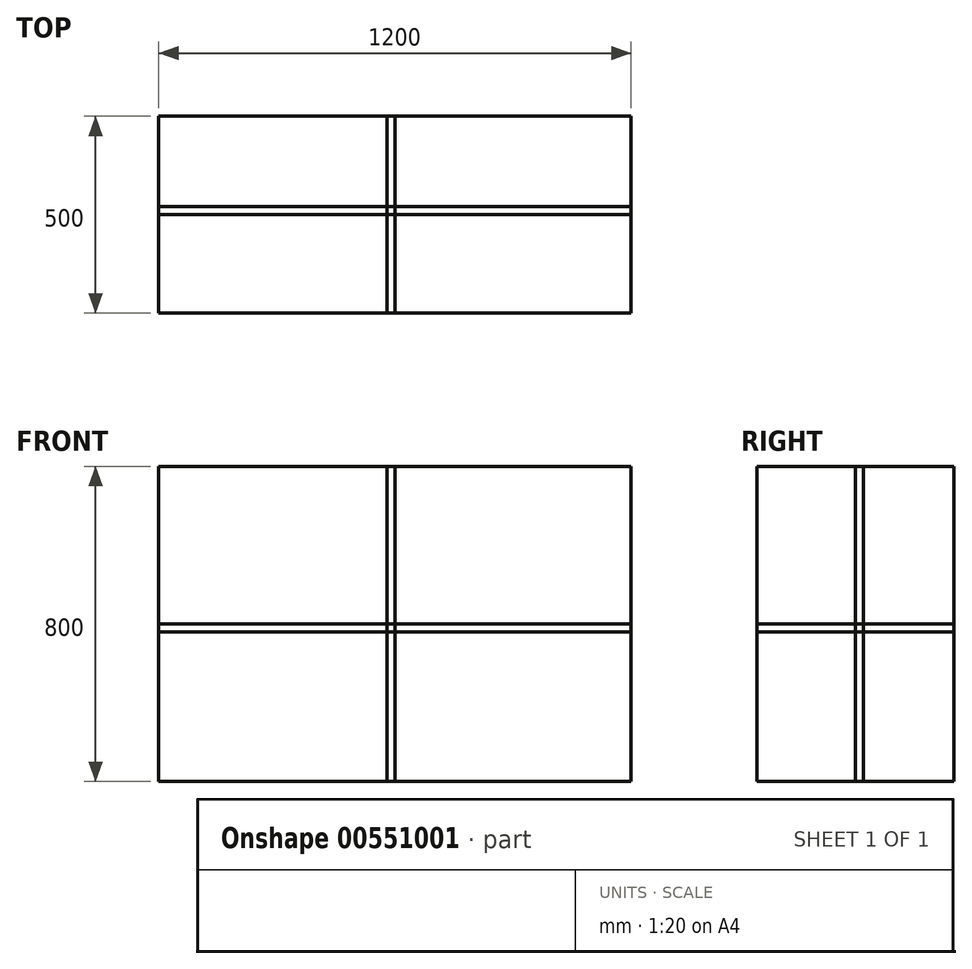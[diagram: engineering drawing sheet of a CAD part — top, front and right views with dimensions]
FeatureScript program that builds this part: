
annotation { "Feature Type Name" : "Feature", "Feature Type Description" : "" }
export const myFeature = defineFeature(function(context is Context, id is Id, definition is map)
    precondition{}
    {
        {
            var Q0;
            Q0=qCreatedBy(makeId("Top.planeOp"),FACE);
            var sketch = newSketch(context, id + "F0", { "sketchPlane" : qUnion([Q0])});
            skLineSegment(sketch, "E0.bottom", {"start": v(600, 250) * mm, "end": v(-600, 250) * mm});
            skLineSegment(sketch, "E0.top", {"start": v(600, -250) * mm, "end": v(-600, -250) * mm});
            skLineSegment(sketch, "E0.left", {"start": v(600, 250) * mm, "end": v(600, -250) * mm});
            skLineSegment(sketch, "E0.right", {"start": v(-600, 250) * mm, "end": v(-600, -250) * mm});
            skPoint(sketch, "E0.middle", {"position": v(0, 0) * mm});
            skSolve(sketch);
        }
        {
            var Q0;
            Q0 = qSketchRegion(id + "F0", true);
            extrude(context, id + "F1", {"entities" : qUnion([Q0]), "oppositeDirection" : true, "depth" : 20 * mm, "offsetDistance" : 25 * mm});
        }
        {
            var Q0;
            Q0=qCreatedBy(makeId("Top.planeOp"),FACE);
            var sketch = newSketch(context, id + "F2", { "sketchPlane" : qUnion([Q0])});
            skLineSegment(sketch, "E1.bottom", {"start": v(600, -250) * mm, "end": v(-600, -250) * mm});
            skLineSegment(sketch, "E1.top", {"start": v(600, 250) * mm, "end": v(-600, 250) * mm});
            skLineSegment(sketch, "E1.left", {"start": v(600, -250) * mm, "end": v(600, 250) * mm});
            skLineSegment(sketch, "E1.right", {"start": v(-600, -250) * mm, "end": v(-600, 250) * mm});
            skPoint(sketch, "E1.middle", {"position": v(0, 0) * mm});
            skSolve(sketch);
        }
        {
            var Q0;
            Q0 = qSketchRegion(id + "F2", true);
            extrude(context, id + "F3", {"entities" : qUnion([Q0]), "oppositeDirection" : true, "depth" : 20 * mm, "offsetDistance" : 25 * mm});
        }
        {
            var Q0;
            Q0=qCreatedBy(makeId("Front.planeOp"),FACE);
            var sketch = newSketch(context, id + "F4", { "sketchPlane" : qUnion([Q0])});
            skLineSegment(sketch, "E2.bottom", {"start": v(600, -400) * mm, "end": v(-600, -400) * mm});
            skLineSegment(sketch, "E2.top", {"start": v(600, 400) * mm, "end": v(-600, 400) * mm});
            skLineSegment(sketch, "E2.left", {"start": v(600, -400) * mm, "end": v(600, 400) * mm});
            skLineSegment(sketch, "E2.right", {"start": v(-600, -400) * mm, "end": v(-600, 400) * mm});
            skPoint(sketch, "E2.middle", {"position": v(0, 0) * mm});
            skSolve(sketch);
        }
        {
            var Q0;
            Q0 = qSketchRegion(id + "F4", true);
            extrude(context, id + "F5", {"entities" : qUnion([Q0]), "oppositeDirection" : true, "depth" : 20 * mm, "offsetDistance" : 25 * mm});
        }
        {
            var Q0;
            Q0=qCreatedBy(makeId("Front.planeOp"),FACE);
            var sketch = newSketch(context, id + "F6", { "sketchPlane" : qUnion([Q0])});
            skLineSegment(sketch, "E3.bottom", {"start": v(600, -400) * mm, "end": v(-600, -400) * mm});
            skLineSegment(sketch, "E3.top", {"start": v(600, 400) * mm, "end": v(-600, 400) * mm});
            skLineSegment(sketch, "E3.left", {"start": v(600, -400) * mm, "end": v(600, 400) * mm});
            skLineSegment(sketch, "E3.right", {"start": v(-600, -400) * mm, "end": v(-600, 400) * mm});
            skPoint(sketch, "E3.middle", {"position": v(0, 0) * mm});
            skSolve(sketch);
        }
        {
            var Q0;
            Q0 = qSketchRegion(id + "F6", true);
            extrude(context, id + "F7", {"entities" : qUnion([Q0]), "oppositeDirection" : true, "depth" : 20 * mm, "offsetDistance" : 25 * mm});
        }
        {
            var Q0;
            Q0=qCreatedBy(makeId("Right.planeOp"),FACE);
            var sketch = newSketch(context, id + "F8", { "sketchPlane" : qUnion([Q0])});
            skLineSegment(sketch, "E4.bottom", {"start": v(250, -400) * mm, "end": v(-250, -400) * mm});
            skLineSegment(sketch, "E4.top", {"start": v(250, 400) * mm, "end": v(-250, 400) * mm});
            skLineSegment(sketch, "E4.left", {"start": v(250, -400) * mm, "end": v(250, 400) * mm});
            skLineSegment(sketch, "E4.right", {"start": v(-250, -400) * mm, "end": v(-250, 400) * mm});
            skPoint(sketch, "E4.middle", {"position": v(0, 0) * mm});
            skSolve(sketch);
        }
        {
            var Q0;
            Q0 = qSketchRegion(id + "F8", true);
            extrude(context, id + "F9", {"entities" : qUnion([Q0]), "oppositeDirection" : true, "depth" : 20 * mm, "offsetDistance" : 25 * mm});
        }
        {
            var Q0;
            Q0=qCreatedBy(makeId("Right.planeOp"),FACE);
            var sketch = newSketch(context, id + "F10", { "sketchPlane" : qUnion([Q0])});
            skLineSegment(sketch, "E5.bottom", {"start": v(250, -400) * mm, "end": v(-250, -400) * mm});
            skLineSegment(sketch, "E5.top", {"start": v(250, 400) * mm, "end": v(-250, 400) * mm});
            skLineSegment(sketch, "E5.left", {"start": v(250, -400) * mm, "end": v(250, 400) * mm});
            skLineSegment(sketch, "E5.right", {"start": v(-250, -400) * mm, "end": v(-250, 400) * mm});
            skPoint(sketch, "E5.middle", {"position": v(0, 0) * mm});
            skSolve(sketch);
        }
        {
            var Q0;
            Q0 = qSketchRegion(id + "F10", true);
            extrude(context, id + "F11", {"entities" : qUnion([Q0]), "oppositeDirection" : true, "depth" : 20 * mm, "offsetDistance" : 25 * mm});
        }
    });
